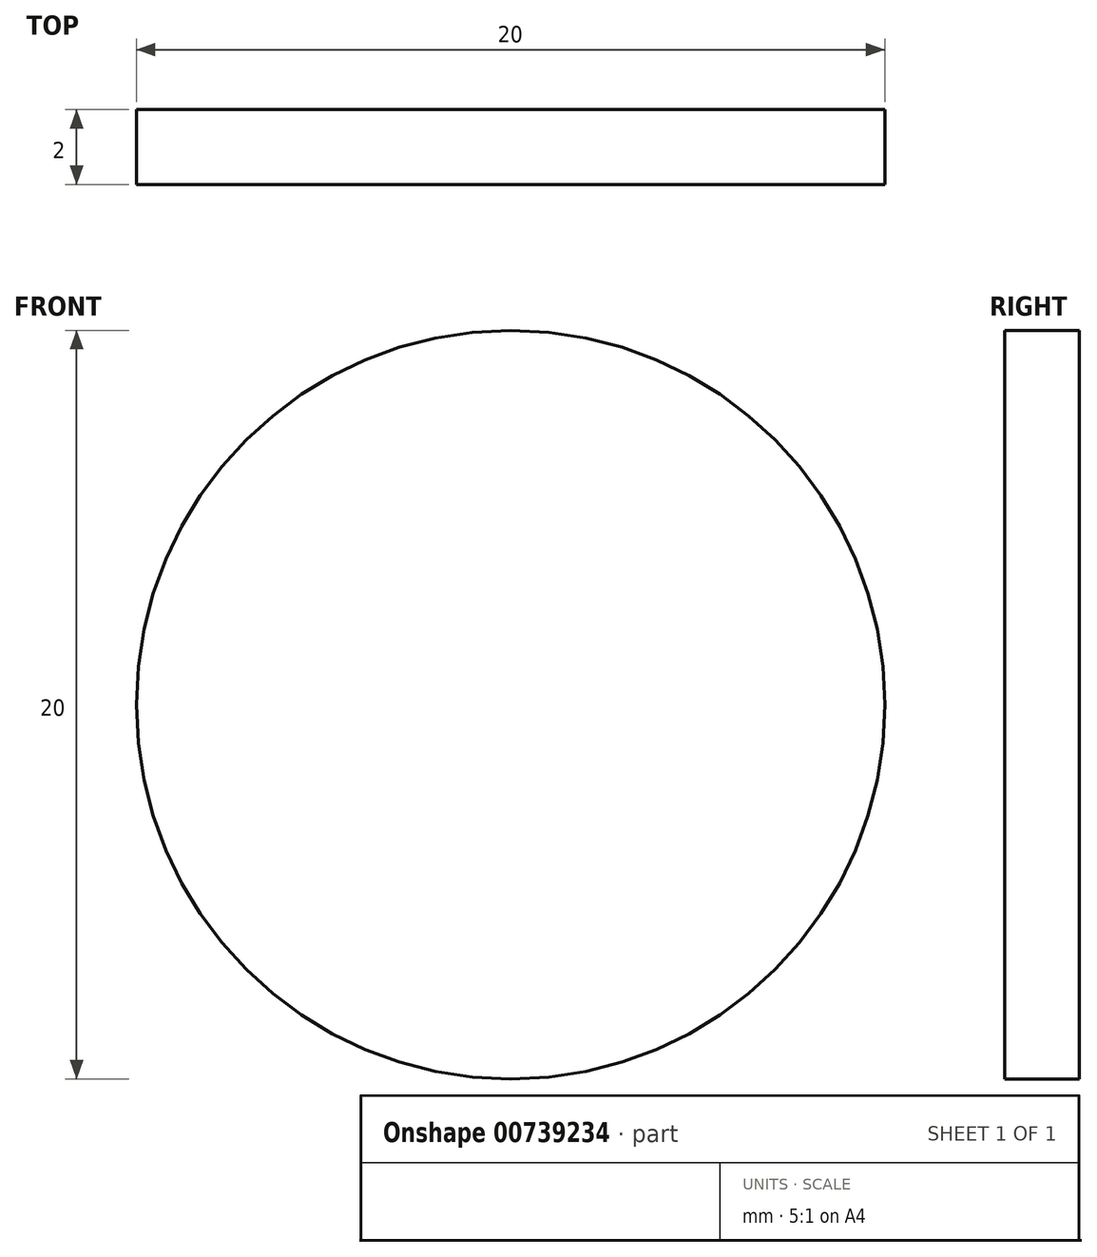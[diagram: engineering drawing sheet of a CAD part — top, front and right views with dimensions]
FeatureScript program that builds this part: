
annotation { "Feature Type Name" : "Feature", "Feature Type Description" : "" }
export const myFeature = defineFeature(function(context is Context, id is Id, definition is map)
    precondition{}
    {
        {
            var Q0;
            Q0=qCreatedBy(makeId("Front.planeOp"),FACE);
            var sketch = newSketch(context, id + "F0", { "sketchPlane" : qUnion([Q0])});
            skCircle(sketch, "E0", {"center": v(0, 0) * mm, "radius": 10 * mm});
            skSolve(sketch);
        }
        {
            var Q0;
            Q0 = qSketchRegion(id + "F0", true);
            extrude(context, id + "F1", {"entities" : qUnion([Q0]), "depth" : 2 * mm, "offsetDistance" : 25.4 * mm});
        }
    });
